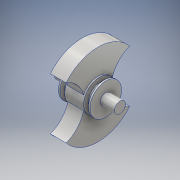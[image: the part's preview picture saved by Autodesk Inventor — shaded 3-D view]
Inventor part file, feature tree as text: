
AUTODESK INVENTOR PART (.ipt)
format: ipt  version: 2016 (Build 200138000, 138)  size: 163,840 bytes
history: native  units: mm
features: sketch x6, extrude x4, revolve x2, other x1
ambient origin geometry x8: Origin, YZ Plane, XZ Plane, XY Plane, X Axis, Y Axis, Z Axis, Center Point
bodies: Body1 (feature_tree)
feature tree (13):
  other  "Sólido1"
  extrude  "Extrusión1"  Depth=38.0mm TaperAngle=0.0deg
  extrude  "Extrusión2"  Depth=10.0mm TaperAngle=0.0deg
  extrude  "Extrusión3"  Depth=12.0mm TaperAngle=0.0deg
  extrude  "Extrusión4"  Depth=20.0mm TaperAngle=0.0deg
  revolve  "Revolución1"  [1 undecoded]
  revolve  "Revolución2"  [1 undecoded]
  sketch  "Boceto1"  dims[d0=7.0mm d1=38.0mm d2=0.0mm]
  sketch  "Boceto2"  dims[d3=44.0mm d6=10.0mm d7=0.0mm]
  sketch  "Boceto3"  dims[d8=20.0mm d9=12.0mm d10=0.0mm]
  sketch  "Boceto4"  dims[d11=14.0mm d12=20.0mm d13=0.0mm]
  sketch  "Boceto6"  dims[d15=1.0mm d16=10.0mm]
  sketch  "Boceto7"  dims[d17=90.0deg d18=1.0mm d19=10.0mm d20=90.0deg d21=52.0mm d22=35.0mm d23=35.0mm]
note: 2 required parameter values undecoded (feature->parameter linkage not recoverable at this tier; creation-order binding heuristic only, values carry confidence <= 0.55)
